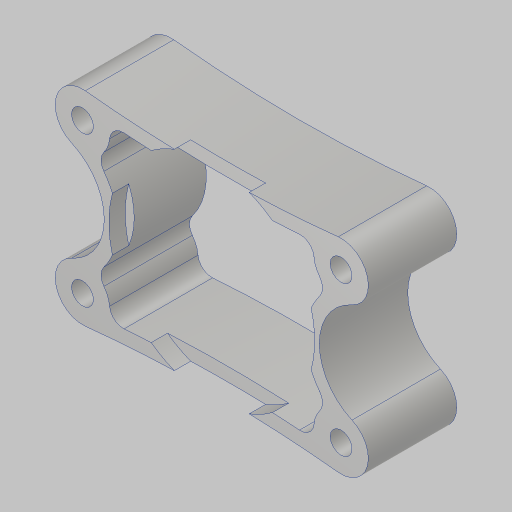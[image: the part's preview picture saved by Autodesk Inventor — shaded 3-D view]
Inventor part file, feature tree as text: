
AUTODESK INVENTOR PART (.ipt)
format: ipt  version: 2023.5 (Build 275446000, 446)  size: 202,240 bytes
history: native  units: in
note: dims shown in document units (in); Inventor stores cm internally (conversion verified against a paired STEP export)
features: sketch x2, extrude x2, fillet x1, hole x1
ambient origin geometry x8: Origin, YZ Plane, XZ Plane, XY Plane, X Axis, Y Axis, Z Axis, Center Point
bodies: Solid1 (feature_tree)
feature tree (6):
  sketch  "Sketch1"  dims[d0=2.375in d1=1.375in d2=0.5in]
  extrude  "Extrusion1"  Depth=0.5in
  fillet  "Fillet1"  Radius=0.5in
  hole  "Hole1"  [1 undecoded]
  extrude  "Extrusion2"  Depth=0.5in
  sketch  "Sketch3"  dims[d3=0.5in d4=0.5in d5=0.5in d6=1.75in d7=0.5in d8=0.5in d9=0.125in d10=0.125in d11=0.812in d12=0.0in d13=0.125in d14=0.201in d15=0.75in d16=0.385in d17=0.25in d18=0.5635in d19=1.0in d20=0.8108in d21=1.89in d22=0.15in d23=0.0in]
note: 1 required parameter value undecoded (feature->parameter linkage not recoverable at this tier; creation-order binding heuristic only, values carry confidence <= 0.55)
